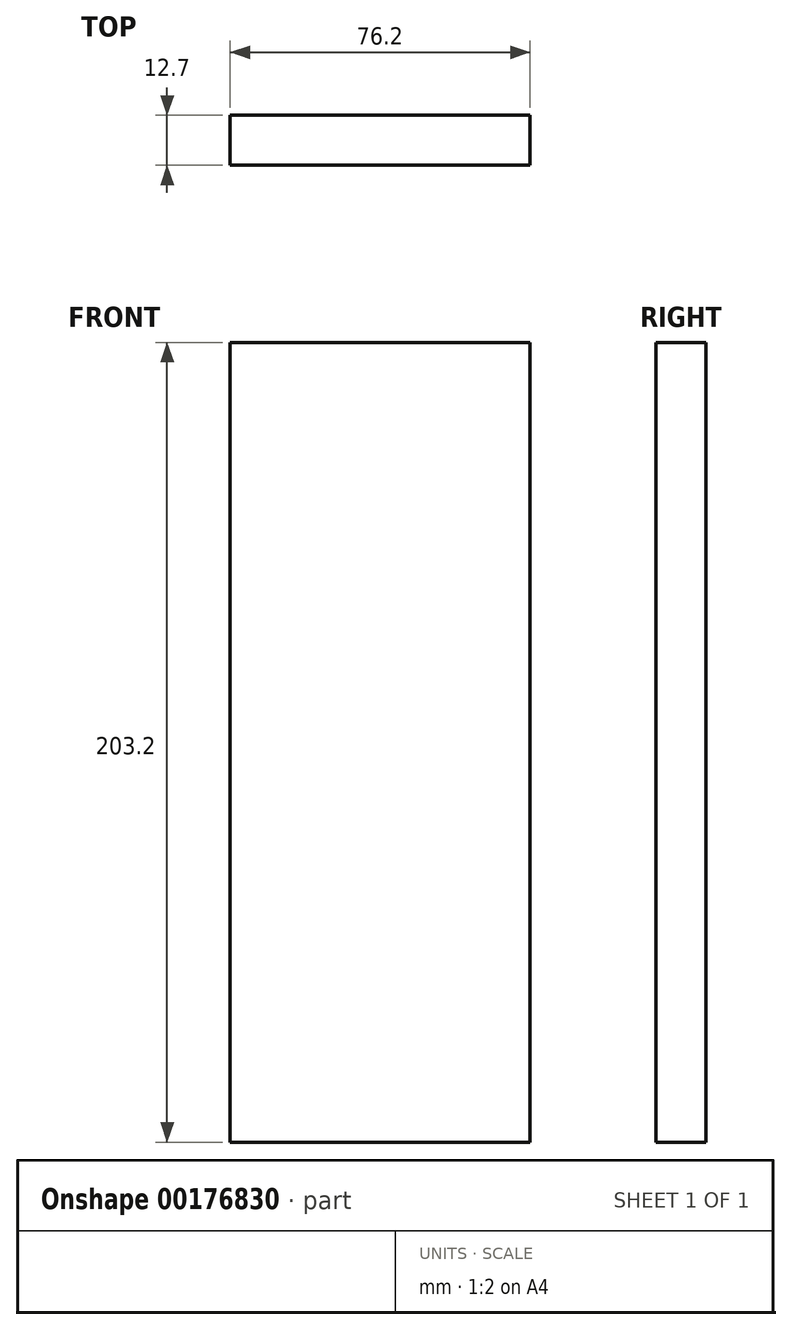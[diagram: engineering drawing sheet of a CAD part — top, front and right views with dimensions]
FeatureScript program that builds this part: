
annotation { "Feature Type Name" : "Feature", "Feature Type Description" : "" }
export const myFeature = defineFeature(function(context is Context, id is Id, definition is map)
    precondition{}
    {
        {
            var Q0;
            Q0=qCreatedBy(makeId("Top.planeOp"),FACE);
            var sketch = newSketch(context, id + "F0", { "sketchPlane" : qUnion([Q0])});
            skLineSegment(sketch, "E0.bottom", {"start": v(-26.51, 1.57) * mm, "end": v(49.69, 1.57) * mm});
            skLineSegment(sketch, "E0.top", {"start": v(-26.51, -11.13) * mm, "end": v(49.69, -11.13) * mm});
            skLineSegment(sketch, "E0.left", {"start": v(-26.51, 1.57) * mm, "end": v(-26.51, -11.13) * mm});
            skLineSegment(sketch, "E0.right", {"start": v(49.69, 1.57) * mm, "end": v(49.69, -11.13) * mm});
            skSolve(sketch);
        }
        {
            var Q0;
            Q0 = qSketchRegion(id + "F0", true);
            extrude(context, id + "F1", {"entities" : qUnion([Q0]), "depth" : 203.2 * mm});
        }
    });
